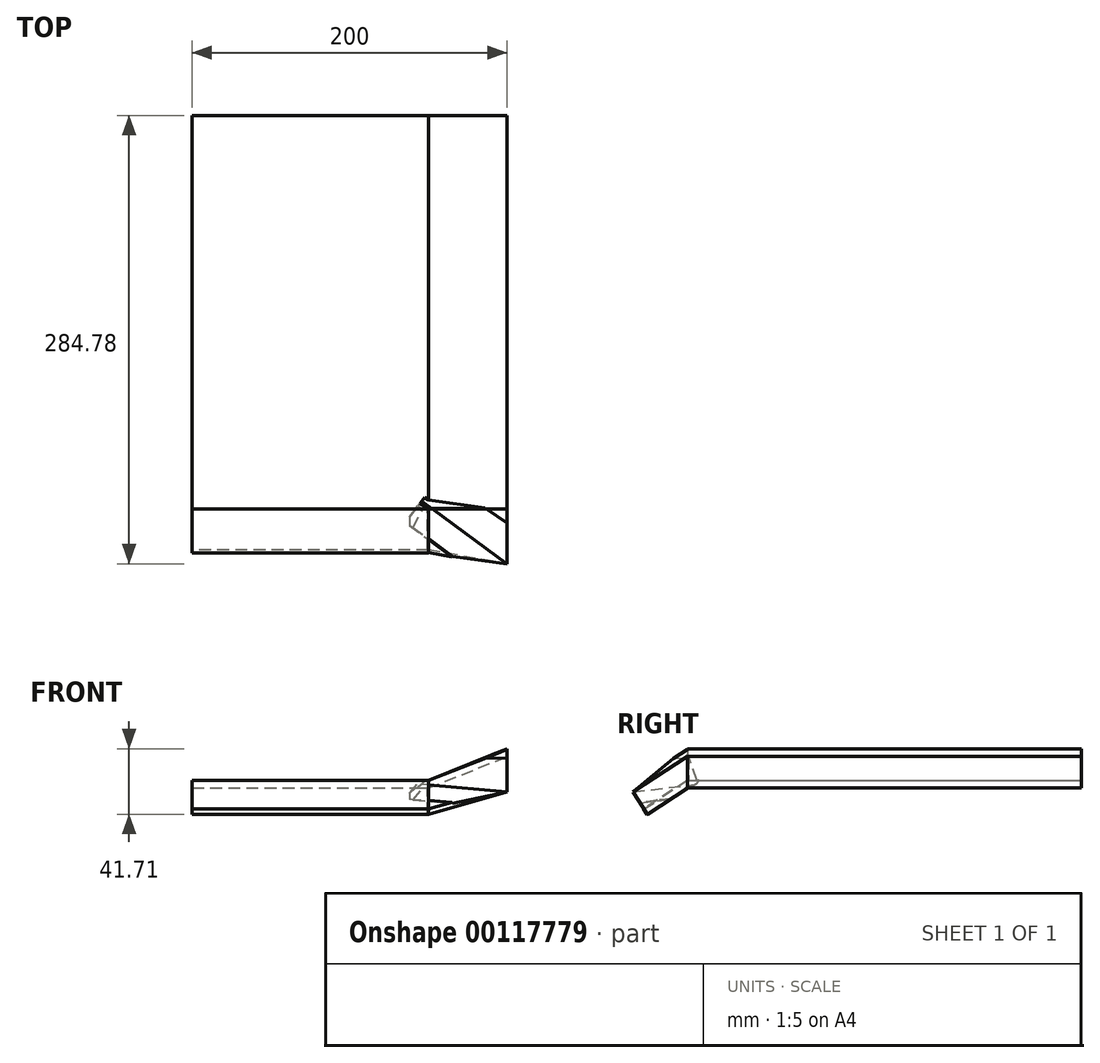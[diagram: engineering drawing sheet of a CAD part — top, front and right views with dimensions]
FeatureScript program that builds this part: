
annotation { "Feature Type Name" : "Feature", "Feature Type Description" : "" }
export const myFeature = defineFeature(function(context is Context, id is Id, definition is map)
    precondition{}
    {
        {
            var Q0;
            Q0=qCreatedBy(makeId("Top.planeOp"),FACE);
            var sketch = newSketch(context, id + "F0", { "sketchPlane" : qUnion([Q0])});
            skLineSegment(sketch, "E0.bottom", {"start": v(0, 0) * mm, "end": v(150, 0) * mm});
            skLineSegment(sketch, "E0.top", {"start": v(0, 250) * mm, "end": v(150, 250) * mm});
            skLineSegment(sketch, "E0.left", {"start": v(0, 0) * mm, "end": v(0, 250) * mm});
            skLineSegment(sketch, "E0.right", {"start": v(150, 0) * mm, "end": v(150, 250) * mm});
            skSolve(sketch);
        }
        {
            var Q0;
            Q0 = qSketchRegion(id + "F0", true);
            extrude(context, id + "F1", {"entities" : qUnion([Q0]), "depth" : 5 * mm});
        }
        {
            var Q0;
            Q0=qCreatedBy(makeId("Right.planeOp"),FACE);
            var sketch = newSketch(context, id + "F2", { "sketchPlane" : qUnion([Q0])});
            skLineSegment(sketch, "E1", {"start": v(0, 0) * mm, "end": v(0, 5) * mm});
            skLineSegment(sketch, "E2", {"start": v(0, 0) * mm, "end": v(-25.86, -16.7) * mm});
            skLineSegment(sketch, "E3", {"start": v(0, 5) * mm, "end": v(-27.98, -13.08) * mm});
            skLineSegment(sketch, "E4", {"start": v(-27.98, -13.08) * mm, "end": v(-25.86, -16.7) * mm});
            skSolve(sketch);
        }
        {
            var Q0;
            Q0 = qSketchRegion(id + "F2", true);
            extrude(context, id + "F3", {"entities" : qUnion([Q0]), "operationType" : NewBodyOperationType.ADD, "depth" : 150 * mm});
        }
        {
            var Q0;
            Q0=qCreatedBy(makeId("Front.planeOp"),FACE);
            var sketch = newSketch(context, id + "F4", { "sketchPlane" : qUnion([Q0])});
            skLineSegment(sketch, "E5", {"start": v(0, 0) * mm, "end": v(150, 0) * mm, "construction": true});
            skLineSegment(sketch, "E6", {"start": v(150, 0) * mm, "end": v(150, -18.63) * mm, "construction": true});
            skLineSegment(sketch, "E7.left", {"start": v(150, 0) * mm, "end": v(150, 5) * mm});
            skLineSegment(sketch, "E8", {"start": v(150, 0) * mm, "end": v(200, 20) * mm});
            skLineSegment(sketch, "E9", {"start": v(200, 20) * mm, "end": v(200, 25) * mm});
            skLineSegment(sketch, "E10", {"start": v(200, 25) * mm, "end": v(150, 5) * mm});
            skPoint(sketch, "E11", {"position": v(175, 10) * mm});
            skSolve(sketch);
        }
        {
            var Q0;
            Q0 = qSketchRegion(id + "F4", true);
            extrude(context, id + "F5", {"entities" : qUnion([Q0]), "operationType" : NewBodyOperationType.ADD, "oppositeDirection" : true, "depth" : 250 * mm});
        }
        {
            var Q0;
            Q0=makeQuery(id+"F3.opExtrude","CAP_VERTEX",VERTEX,{"disambiguationData":[OSD([sQuery(id+"F2.wireOp",EDGE,"E2"),sQuery(id+"F2.wireOp",EDGE,"E4")])],"isStart":false});
            var Q1;
            Q1=makeQuery(id+"F5.boolean.opBoolean","MERGE",VERTEX,{"derivedFrom":[makeQuery(id+"F3.boolean.opBoolean","MERGE",VERTEX,{"derivedFrom":[makeQuery(id+"F1.opExtrude","CAP_VERTEX",VERTEX,{"disambiguationData":[OSD([sQuery(id+"F0.wireOp",EDGE,"E0.bottom"),sQuery(id+"F0.wireOp",EDGE,"E0.right")])],"isStart":true}),makeQuery(id+"F3.opExtrude","CAP_VERTEX",VERTEX,{"disambiguationData":[OSD([sQuery(id+"F2.wireOp",EDGE,"E1"),sQuery(id+"F2.wireOp",EDGE,"E2")])],"isStart":false})]}),makeQuery(id+"F5.opExtrude","CAP_VERTEX",VERTEX,{"disambiguationData":[OSD([sQuery(id+"F4.wireOp",EDGE,"E7.left"),sQuery(id+"F4.wireOp",EDGE,"E8")])],"isStart":true})]});
            var Q2;
            Q2=makeQuery(id+"F5.opExtrude","CAP_VERTEX",VERTEX,{"disambiguationData":[OSD([sQuery(id+"F4.wireOp",EDGE,"E8"),sQuery(id+"F4.wireOp",EDGE,"E9")])],"isStart":true});
            cPlane(context, id + "F6", {"entities" : qUnion([Q0, Q1, Q2]), "cplaneType" : CPlaneType.THREE_POINT, "offset" : 25 * mm, "width" : 150 * mm, "height" : 150 * mm});
        }
        {
            var Q0;
            Q0=qCreatedBy(id+"F6.planeOp",FACE);
            var sketch = newSketch(context, id + "F7", { "sketchPlane" : qUnion([Q0])});
            skLineSegment(sketch, "E12.bottom", {"start": v(141.66, -30.46) * mm, "end": v(200.63, -30.46) * mm});
            skLineSegment(sketch, "E12.top", {"start": v(141.66, 15.85) * mm, "end": v(200.63, 15.85) * mm});
            skLineSegment(sketch, "E12.left", {"start": v(141.66, -30.46) * mm, "end": v(141.66, 15.85) * mm});
            skLineSegment(sketch, "E12.right", {"start": v(200.63, -30.46) * mm, "end": v(200.63, 15.85) * mm});
            skSolve(sketch);
        }
        {
            var Q0;
            Q0 = qSketchRegion(id + "F7", true);
            extrude(context, id + "F8", {"entities" : qUnion([Q0]), "operationType" : NewBodyOperationType.ADD, "depth" : 3.62 * mm});
        }
        {
            var Q0;
            {var subQ2=sQuery(id+"F4.wireOp",EDGE,"E10");var subQ3=sQuery(id+"F0.wireOp",EDGE,"E0.top");Q0=makeQuery(id+"F8.boolean.opBoolean","SPLIT",FACE,{"disambiguationData":[TD([makeQuery(id+"F1.opExtrude","SWEPT_FACE",FACE,{"disambiguationData":[OSD([subQ3])]})])],"derivedFrom":makeQuery(id+"F5.opExtrude","SWEPT_FACE",FACE,{"disambiguationData":[OSD([subQ2])]})});}
            var sketch = newSketch(context, id + "F9", { "sketchPlane" : qUnion([Q0])});
            skLineSegment(sketch, "E13.bottom", {"start": v(207.43, 23.8) * mm, "end": v(141.13, 23.8) * mm});
            skLineSegment(sketch, "E13.top", {"start": v(207.43, 0) * mm, "end": v(141.13, 0) * mm});
            skLineSegment(sketch, "E13.left", {"start": v(207.43, 23.8) * mm, "end": v(207.43, 0) * mm});
            skLineSegment(sketch, "E13.right", {"start": v(141.13, 23.8) * mm, "end": v(141.13, 0) * mm});
            skSolve(sketch);
        }
        {
            var Q0;
            Q0 = qSketchRegion(id + "F9", true);
            extrude(context, id + "F10", {"entities" : qUnion([Q0]), "operationType" : NewBodyOperationType.REMOVE, "depth" : 25 * mm});
        }
        {
            var Q0;
            Q0=makeQuery(id+"F1.opExtrude","CAP_FACE",FACE,{"disambiguationData":[OSD([sQuery(id+"F0.wireOp",EDGE,"E0.bottom"),sQuery(id+"F0.wireOp",EDGE,"E0.top"),sQuery(id+"F0.wireOp",EDGE,"E0.left"),sQuery(id+"F0.wireOp",EDGE,"E0.right")])],"isStart":false});
            var sketch = newSketch(context, id + "F11", { "sketchPlane" : qUnion([Q0])});
            skLineSegment(sketch, "E14.bottom", {"start": v(140.23, 36.4) * mm, "end": v(150, 36.4) * mm});
            skLineSegment(sketch, "E14.top", {"start": v(140.23, 0) * mm, "end": v(150, 0) * mm});
            skLineSegment(sketch, "E14.left", {"start": v(140.23, 36.4) * mm, "end": v(140.23, 0) * mm});
            skLineSegment(sketch, "E14.right", {"start": v(150, 36.4) * mm, "end": v(150, 0) * mm});
            skSolve(sketch);
        }
        {
            var Q0;
            Q0 = qSketchRegion(id + "F11", true);
            extrude(context, id + "F12", {"entities" : qUnion([Q0]), "operationType" : NewBodyOperationType.REMOVE, "depth" : 25 * mm});
        }
        {
            var Q0;
            {var subQ1=sQuery(id+"F4.wireOp",EDGE,"E9");Q0=makeQuery(id+"F8.boolean.opBoolean","SPLIT",FACE,{"disambiguationData":[TD([makeQuery(id+"F1.opExtrude","SWEPT_FACE",FACE,{"disambiguationData":[OSD([sQuery(id+"F0.wireOp",EDGE,"E0.top")])]})])],"derivedFrom":makeQuery(id+"F5.opExtrude","SWEPT_FACE",FACE,{"disambiguationData":[OSD([subQ1])]})});}
            var sketch = newSketch(context, id + "F13", { "sketchPlane" : qUnion([Q0])});
            skLineSegment(sketch, "E15.bottom", {"start": v(32.7, 40.36) * mm, "end": v(-59.28, 40.36) * mm});
            skLineSegment(sketch, "E15.top", {"start": v(32.7, -13.1) * mm, "end": v(-59.28, -13.1) * mm});
            skLineSegment(sketch, "E15.left", {"start": v(32.7, 40.36) * mm, "end": v(32.7, -13.1) * mm});
            skLineSegment(sketch, "E15.right", {"start": v(-59.28, 40.36) * mm, "end": v(-59.28, -13.1) * mm});
            skSolve(sketch);
        }
        {
            var Q0;
            Q0 = qSketchRegion(id + "F13", true);
            extrude(context, id + "F14", {"entities" : qUnion([Q0]), "operationType" : NewBodyOperationType.REMOVE, "depth" : 25 * mm});
        }
        {
            var Q0;
            Q0=makeQuery(id+"F5.boolean.opBoolean","MERGE",VERTEX,{"derivedFrom":[makeQuery(id+"F3.boolean.opBoolean","MERGE",VERTEX,{"derivedFrom":[makeQuery(id+"F1.opExtrude","CAP_VERTEX",VERTEX,{"disambiguationData":[OSD([sQuery(id+"F0.wireOp",EDGE,"E0.bottom"),sQuery(id+"F0.wireOp",EDGE,"E0.right")])],"isStart":false}),makeQuery(id+"F3.opExtrude","CAP_VERTEX",VERTEX,{"disambiguationData":[OSD([sQuery(id+"F2.wireOp",EDGE,"E1"),sQuery(id+"F2.wireOp",EDGE,"E3")])],"isStart":false})]}),makeQuery(id+"F5.opExtrude","CAP_VERTEX",VERTEX,{"disambiguationData":[OSD([sQuery(id+"F4.wireOp",EDGE,"E7.left"),sQuery(id+"F4.wireOp",EDGE,"E10")])],"isStart":true})]});
            var Q1;
            {var subQ1=makeQuery(id+"F1.opExtrude","SWEPT_FACE",FACE,{"disambiguationData":[OSD([sQuery(id+"F0.wireOp",EDGE,"E0.right")])]});var subQ5=sQuery(id+"F7.wireOp",EDGE,"E12.bottom");var subQ6=makeQuery(id+"F8.opExtrude","SWEPT_FACE",FACE,{"disambiguationData":[OSD([subQ5])]});var subQ7=sQuery(id+"F7.wireOp",EDGE,"E12.right");var subQ8=makeQuery(id+"F8.opExtrude","SWEPT_FACE",FACE,{"disambiguationData":[OSD([subQ7])]});var subQ9=sQuery(id+"F7.wireOp",EDGE,"E12.left");var subQ10=sQuery(id+"F7.wireOp",EDGE,"E12.top");var subQ11=makeQuery(id+"F8.opExtrude","CAP_FACE",FACE,{"disambiguationData":[OSD([subQ5,subQ10,subQ9,subQ7])],"isStart":false});Q1=makeQuery(id+"F14.boolean.opBoolean","INTERSECT",VERTEX,{"derivedFrom":[makeQuery(id+"F8.boolean.opBoolean","SPLIT",FACE,{"disambiguationData":[TD([subQ8])],"derivedFrom":subQ6}),makeQuery(id+"F10.boolean.opBoolean","SPLIT",FACE,{"disambiguationData":[TD([subQ1])],"derivedFrom":subQ11}),makeQuery(id+"F14.opExtrude","CAP_FACE",FACE,{"disambiguationData":[OSD([sQuery(id+"F13.wireOp",EDGE,"E15.bottom"),sQuery(id+"F13.wireOp",EDGE,"E15.top"),sQuery(id+"F13.wireOp",EDGE,"E15.left"),sQuery(id+"F13.wireOp",EDGE,"E15.right")])],"isStart":true})]});}
            cPlane(context, id + "F15", {"entities" : qUnion([Q0, Q1]), "cplaneType" : CPlaneType.MID_PLANE, "offset" : 25 * mm, "width" : 150 * mm, "height" : 150 * mm});
        }
        {
            var Q0;
            Q0=qCreatedBy(id+"F15.planeOp",FACE);
            var sketch = newSketch(context, id + "F16", { "sketchPlane" : qUnion([Q0])});
            skLineSegment(sketch, "E16", {"start": v(89.87, 14.5) * mm, "end": v(66.8, 0) * mm});
            skLineSegment(sketch, "E17", {"start": v(66.8, 0) * mm, "end": v(116.42, 42.68) * mm});
            skLineSegment(sketch, "E18", {"start": v(116.42, 42.68) * mm, "end": v(89.87, 14.5) * mm});
            skSolve(sketch);
        }
        {
            var Q0;
            Q0=makeQuery(id+"F16.imprint","IMPRINT",FACE,{"disambiguationData":[TD([[makeQuery(id+"F16.imprint","IMPRINT",EDGE,{"derivedFrom":sQuery(id+"F16.wireOp",EDGE,"E16")}),-1.0]])]});
            extrude(context, id + "F17", {"entities" : qUnion([Q0]), "operationType" : NewBodyOperationType.REMOVE, "depth" : 42.8 * mm});
        }
        {
            var Q0;
            {var subQ0=sQuery(id+"F7.wireOp",EDGE,"E12.bottom");var subQ1=sQuery(id+"F16.wireOp",EDGE,"E16");var subQ2=sQuery(id+"F16.wireOp",EDGE,"E18");Q0=makeQuery(id+"F17.boolean.opBoolean","COPY",FACE,{"disambiguationData":[TD([makeQuery(id+"F8.opExtrude","SWEPT_FACE",FACE,{"disambiguationData":[OSD([subQ0])]})])],"derivedFrom":makeQuery(id+"F17.opExtrude","CAP_FACE",FACE,{"disambiguationData":[OSD([subQ1,sQuery(id+"F16.wireOp",EDGE,"E17"),subQ2])],"isStart":true})});}
            extrude(context, id + "F18", {"entities" : qUnion([Q0]), "operationType" : NewBodyOperationType.REMOVE, "oppositeDirection" : true, "depth" : 37.26 * mm});
        }
    });
